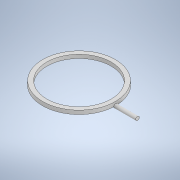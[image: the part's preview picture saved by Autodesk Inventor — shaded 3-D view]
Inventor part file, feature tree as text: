
AUTODESK INVENTOR PART (.ipt)
format: ipt  version: 2022 (Build 260153000, 153)  size: 144,384 bytes
history: native  units: in
note: dims shown in document units (in); Inventor stores cm internally (conversion verified against a paired STEP export)
features: sketch x6, extrude x5, revolve x1
ambient origin geometry x8: Origin, YZ Plane, XZ Plane, XY Plane, X Axis, Y Axis, Z Axis, Center Point
bodies: Solid1 (feature_tree)
feature tree (12):
  revolve  "Revolution1"  Angle=180.0deg
  extrude  "Extrusion1"  Depth=1.1in
  extrude  "Extrusion2"  Depth=0.125in
  extrude  "Extrusion3"  Depth=2.0in
  sketch  "Sketch5"  dims[d11=1.125in d12=0.0in d13=1.125in d14=0.0in]
  extrude  "Extrusion4"  Depth=1.125in TaperAngle=0.0deg
  extrude  "Extrusion5"  Depth=0.0625in
  sketch  "Sketch1"  dims[d0=1.25in d1=180.0deg]
  sketch  "Sketch2"  dims[d2=180.0deg d4=1.1in]
  sketch  "Sketch3"  dims[d5=0.125in d6=0.0in d7=0.125in]
  sketch  "Sketch4"  dims[d8=2.0in d9=0.0in d10=0.125in]
  sketch  "Sketch6"  dims[d15=0.0625in d16=0.0in d17=0.5in d18=0.0344in]
